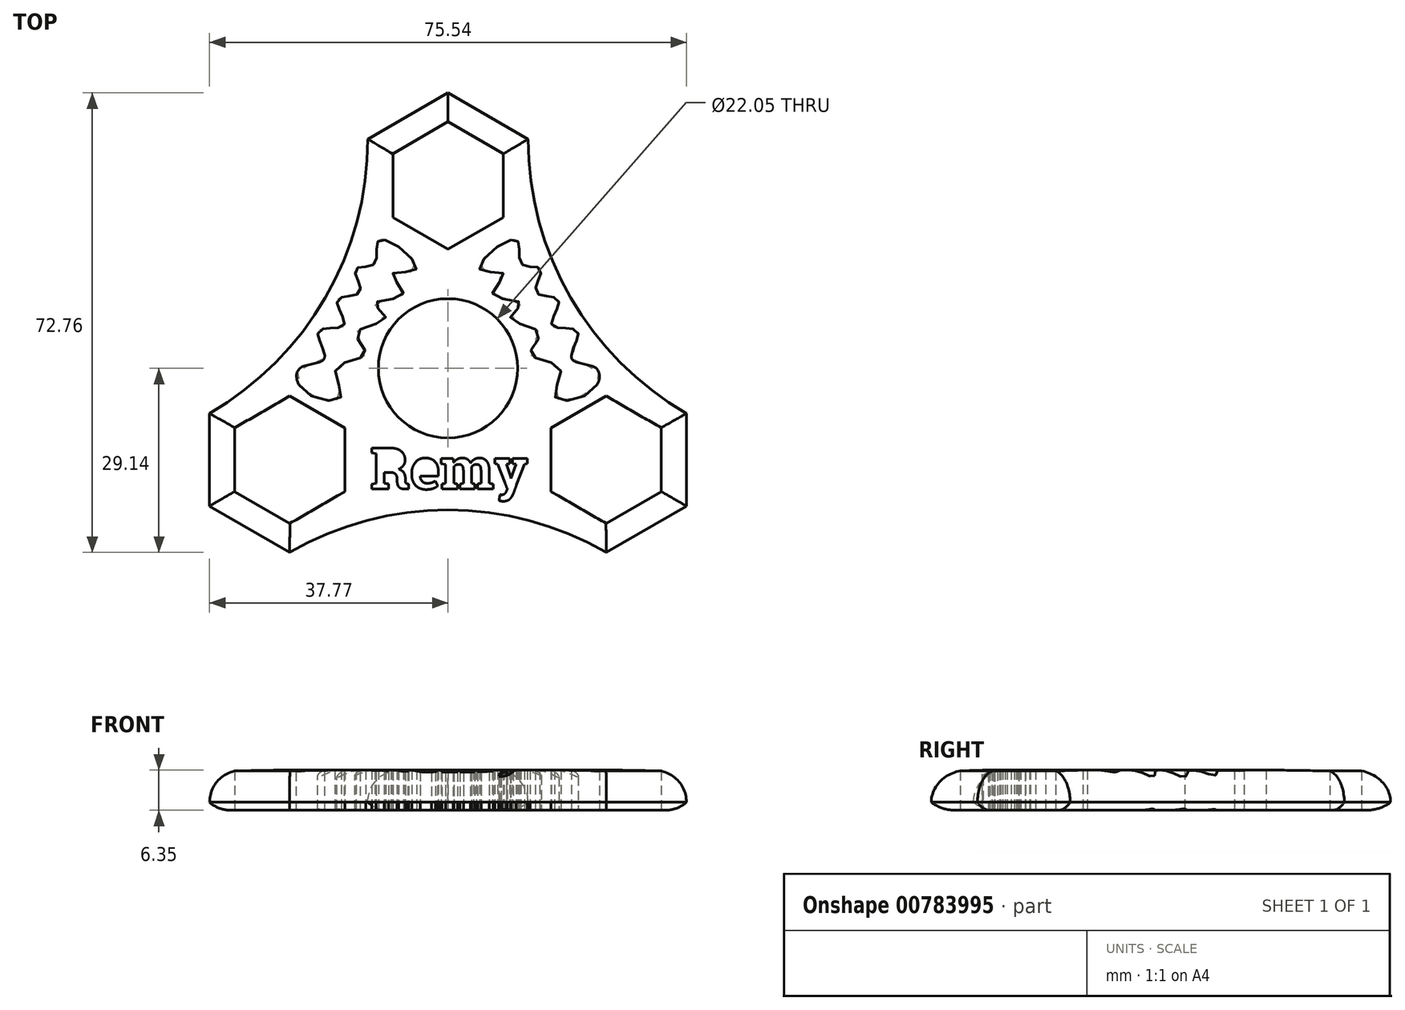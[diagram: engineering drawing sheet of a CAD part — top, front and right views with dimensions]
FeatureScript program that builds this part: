
annotation { "Feature Type Name" : "Feature", "Feature Type Description" : "" }
export const myFeature = defineFeature(function(context is Context, id is Id, definition is map)
    precondition{}
    {
        {
            var Q0;
            Q0=qCreatedBy(makeId("Top.planeOp"),FACE);
            var sketch = newSketch(context, id + "F0", { "sketchPlane" : qUnion([Q0])});
            skCircle(sketch, "E0", {"center": v(0, 0) * mm, "radius": 11.02 * mm});
            skCircle(sketch, "E1", {"center": v(0, 0) * mm, "radius": 14.29 * mm});
            skCircle(sketch, "E2.cCircle", {"center": v(0, 28.95) * mm, "radius": 8.73 * mm, "construction": true});
            skLineSegment(sketch, "E2.0", {"start": v(-8.73, 34) * mm, "end": v(0, 39.03) * mm});
            skLineSegment(sketch, "E2.1", {"start": v(0, 39.03) * mm, "end": v(8.73, 34) * mm});
            skLineSegment(sketch, "E2.2", {"start": v(8.73, 34) * mm, "end": v(8.73, 23.91) * mm});
            skLineSegment(sketch, "E2.3", {"start": v(8.73, 23.91) * mm, "end": v(0, 18.87) * mm});
            skLineSegment(sketch, "E2.4", {"start": v(0, 18.87) * mm, "end": v(-8.73, 23.91) * mm});
            skLineSegment(sketch, "E2.5", {"start": v(-8.73, 23.91) * mm, "end": v(-8.73, 34) * mm});
            skPoint(sketch, "E2.0.midPoint", {"position": v(-4.37, 36.51) * mm});
            skCircle(sketch, "E3.cCircle", {"center": v(0, 28.95) * mm, "radius": 12.7 * mm, "construction": true});
            skLineSegment(sketch, "E3.0", {"start": v(-12.7, 36.28) * mm, "end": v(0, 43.62) * mm});
            skLineSegment(sketch, "E3.1", {"start": v(0, 43.62) * mm, "end": v(12.7, 36.28) * mm});
            skLineSegment(sketch, "E3.2", {"start": v(12.7, 36.28) * mm, "end": v(12.7, 21.62) * mm});
            skLineSegment(sketch, "E3.3", {"start": v(12.7, 21.62) * mm, "end": v(0, 14.29) * mm});
            skLineSegment(sketch, "E3.4", {"start": v(0, 14.29) * mm, "end": v(-12.7, 21.62) * mm});
            skLineSegment(sketch, "E3.5", {"start": v(-12.7, 21.62) * mm, "end": v(-12.7, 36.28) * mm});
            skPoint(sketch, "E3.0.midPoint", {"position": v(-6.35, 39.95) * mm});
            skLineSegment(sketch, "E4.1.0", {"start": v(-37.77, -21.8) * mm, "end": v(-37.77, -7.14) * mm});
            skLineSegment(sketch, "E4.1.1", {"start": v(-25.07, 0.19) * mm, "end": v(-12.37, -7.14) * mm});
            skLineSegment(sketch, "E4.1.2", {"start": v(-16.34, -19.52) * mm, "end": v(-25.07, -24.56) * mm});
            skLineSegment(sketch, "E4.1.3", {"start": v(-12.37, -21.8) * mm, "end": v(-25.07, -29.14) * mm});
            skLineSegment(sketch, "E4.1.4", {"start": v(-37.77, -7.14) * mm, "end": v(-25.07, 0.19) * mm});
            skLineSegment(sketch, "E4.1.5", {"start": v(-33.8, -9.44) * mm, "end": v(-25.07, -4.4) * mm});
            skLineSegment(sketch, "E4.1.6", {"start": v(-33.8, -19.52) * mm, "end": v(-33.8, -9.44) * mm});
            skLineSegment(sketch, "E4.1.7", {"start": v(-25.07, -4.4) * mm, "end": v(-16.34, -9.44) * mm});
            skCircle(sketch, "E4.1.8", {"center": v(-25.07, -14.48) * mm, "radius": 12.7 * mm, "construction": true});
            skLineSegment(sketch, "E4.1.9", {"start": v(-25.07, -24.56) * mm, "end": v(-33.8, -19.52) * mm});
            skLineSegment(sketch, "E4.1.10", {"start": v(-16.34, -9.44) * mm, "end": v(-16.34, -19.52) * mm});
            skPoint(sketch, "E4.1.11", {"position": v(-31.42, -25.47) * mm});
            skCircle(sketch, "E4.1.12", {"center": v(-25.07, -14.48) * mm, "radius": 8.73 * mm, "construction": true});
            skLineSegment(sketch, "E4.1.13", {"start": v(-12.37, -7.14) * mm, "end": v(-12.37, -21.8) * mm});
            skPoint(sketch, "E4.1.14", {"position": v(-29.44, -22.04) * mm});
            skLineSegment(sketch, "E4.1.15", {"start": v(-25.07, -29.14) * mm, "end": v(-37.77, -21.8) * mm});
            skLineSegment(sketch, "E4.2.0", {"start": v(37.77, -21.8) * mm, "end": v(25.07, -29.14) * mm});
            skLineSegment(sketch, "E4.2.1", {"start": v(12.37, -21.8) * mm, "end": v(12.37, -7.14) * mm});
            skLineSegment(sketch, "E4.2.2", {"start": v(25.07, -4.4) * mm, "end": v(33.8, -9.44) * mm});
            skLineSegment(sketch, "E4.2.3", {"start": v(25.07, 0.19) * mm, "end": v(37.77, -7.14) * mm});
            skLineSegment(sketch, "E4.2.4", {"start": v(25.07, -29.14) * mm, "end": v(12.37, -21.8) * mm});
            skLineSegment(sketch, "E4.2.5", {"start": v(25.07, -24.56) * mm, "end": v(16.34, -19.52) * mm});
            skLineSegment(sketch, "E4.2.6", {"start": v(33.8, -19.52) * mm, "end": v(25.07, -24.56) * mm});
            skLineSegment(sketch, "E4.2.7", {"start": v(16.34, -19.52) * mm, "end": v(16.34, -9.44) * mm});
            skCircle(sketch, "E4.2.8", {"center": v(25.07, -14.48) * mm, "radius": 12.7 * mm, "construction": true});
            skLineSegment(sketch, "E4.2.9", {"start": v(33.8, -9.44) * mm, "end": v(33.8, -19.52) * mm});
            skLineSegment(sketch, "E4.2.10", {"start": v(16.34, -9.44) * mm, "end": v(25.07, -4.4) * mm});
            skPoint(sketch, "E4.2.11", {"position": v(37.77, -14.48) * mm});
            skCircle(sketch, "E4.2.12", {"center": v(25.07, -14.48) * mm, "radius": 8.73 * mm, "construction": true});
            skLineSegment(sketch, "E4.2.13", {"start": v(12.37, -7.14) * mm, "end": v(25.07, 0.19) * mm});
            skPoint(sketch, "E4.2.14", {"position": v(33.8, -14.48) * mm});
            skLineSegment(sketch, "E4.2.15", {"start": v(37.77, -7.14) * mm, "end": v(37.77, -21.8) * mm});
            skArc(sketch, "E5", {"start": v(-37.77, -7.14) * mm, "mid": v(-19.42, 11.21) * mm, "end": v(-12.7, 36.28) * mm});
            skArc(sketch, "E6", {"start": v(12.7, 36.28) * mm, "mid": v(19.42, 11.21) * mm, "end": v(37.77, -7.14) * mm});
            skArc(sketch, "E7", {"start": v(25.07, -29.14) * mm, "mid": v(0, -22.42) * mm, "end": v(-25.07, -29.14) * mm});
            skSolve(sketch);
        }
        {
            var Q0;
            Q0 = qSketchRegion(id + "F0", true);
            var Q1;
            Q1=makeQuery(id+"F0.imprint","IMPRINT",FACE,{"disambiguationData":[TD([[makeQuery(id+"F0.imprint","IMPRINT",EDGE,{"derivedFrom":sQuery(id+"F0.wireOp",EDGE,"E0")}),-1.0]])]});
            extrude(context, id + "F1", {"entities" : qUnion([Q0, Q1]), "depth" : 6.35 * mm, "offsetDistance" : 25.4 * mm});
        }
        {
            var Q0;
            Q0=qCreatedBy(makeId("Top.planeOp"),FACE);
            var sketch = newSketch(context, id + "F2", { "sketchPlane" : qUnion([Q0])});
            skText(sketch, "E8", { "text": "Remy", "fontName": "RobotoSlab-Bold.ttf"});
            const initialGuessF2  = {"E8": [-0.01232, -0.01911, 1, 0, 0.00657]};
            skSetInitialGuess(sketch, initialGuessF2);
            skSolve(sketch);
        }
        {
            var Q0;
            Q0 = qSketchRegion(id + "F2", true);
            extrude(context, id + "F3", {"entities" : qUnion([Q0]), "operationType" : NewBodyOperationType.REMOVE, "endBound" : BoundingType.THROUGH_ALL, "depth" : 25.4 * mm, "offsetDistance" : 25.4 * mm});
        }
        {
            var Q0;
            Q0=qCreatedBy(makeId("Top.planeOp"),FACE);
            var sketch = newSketch(context, id + "F4", { "sketchPlane" : qUnion([Q0])});
            skSolve(sketch);
        }
        {
            var Q0;
            Q0 = qSketchRegion(id + "F4", true);
            var Q1;
            Q1=makeQuery(id+"F3.boolean.opBoolean","SPLIT",FACE,{"disambiguationData":[TD([makeQuery(id+"F3.opExtrude","SWEPT_FACE",FACE,{"disambiguationData":[OSD([sQuery(id+"F2.wireOp",EDGE,"E8.sketch_text.stroke-29")])]})])],"derivedFrom":makeQuery(id+"F1.opExtrude","CAP_FACE",FACE,{"disambiguationData":[OSD([sQuery(id+"F0.wireOp",EDGE,"E0"),sQuery(id+"F0.wireOp",EDGE,"E2.0"),sQuery(id+"F0.wireOp",EDGE,"E2.1"),sQuery(id+"F0.wireOp",EDGE,"E2.2"),sQuery(id+"F0.wireOp",EDGE,"E2.3"),sQuery(id+"F0.wireOp",EDGE,"E2.4"),sQuery(id+"F0.wireOp",EDGE,"E2.5"),sQuery(id+"F0.wireOp",EDGE,"E3.0"),sQuery(id+"F0.wireOp",EDGE,"E3.1"),sQuery(id+"F0.wireOp",EDGE,"E4.1.0"),sQuery(id+"F0.wireOp",EDGE,"E4.1.2"),sQuery(id+"F0.wireOp",EDGE,"E4.1.5"),sQuery(id+"F0.wireOp",EDGE,"E4.1.6"),sQuery(id+"F0.wireOp",EDGE,"E4.1.7"),sQuery(id+"F0.wireOp",EDGE,"E4.1.9"),sQuery(id+"F0.wireOp",EDGE,"E4.1.10"),sQuery(id+"F0.wireOp",EDGE,"E4.1.15"),sQuery(id+"F0.wireOp",EDGE,"E4.2.0"),sQuery(id+"F0.wireOp",EDGE,"E4.2.2"),sQuery(id+"F0.wireOp",EDGE,"E4.2.5"),sQuery(id+"F0.wireOp",EDGE,"E4.2.6"),sQuery(id+"F0.wireOp",EDGE,"E4.2.7"),sQuery(id+"F0.wireOp",EDGE,"E4.2.9"),sQuery(id+"F0.wireOp",EDGE,"E4.2.10"),sQuery(id+"F0.wireOp",EDGE,"E4.2.15"),sQuery(id+"F0.wireOp",EDGE,"E5"),sQuery(id+"F0.wireOp",EDGE,"E6"),sQuery(id+"F0.wireOp",EDGE,"E7")])],"isStart":false})});
            extrude(context, id + "F5", {"entities" : qUnion([Q0, Q1]), "operationType" : NewBodyOperationType.REMOVE, "endBound" : BoundingType.THROUGH_ALL, "oppositeDirection" : true, "depth" : 25.4 * mm, "offsetDistance" : 25.4 * mm});
        }
        {
            var Q0;
            Q0=qCreatedBy(makeId("Top.planeOp"),FACE);
            var sketch = newSketch(context, id + "F6", { "sketchPlane" : qUnion([Q0])});
            skSolve(sketch);
        }
        {
            var Q0;
            Q0 = qSketchRegion(id + "F6", true);
            var Q1;
            Q1=makeQuery(id+"F3.boolean.opBoolean","SPLIT",FACE,{"disambiguationData":[TD([makeQuery(id+"F3.opExtrude","SWEPT_FACE",FACE,{"disambiguationData":[OSD([sQuery(id+"F2.wireOp",EDGE,"E8.sketch_text.stroke-53")])]})])],"derivedFrom":makeQuery(id+"F1.opExtrude","CAP_FACE",FACE,{"disambiguationData":[OSD([sQuery(id+"F0.wireOp",EDGE,"E0"),sQuery(id+"F0.wireOp",EDGE,"E2.0"),sQuery(id+"F0.wireOp",EDGE,"E2.1"),sQuery(id+"F0.wireOp",EDGE,"E2.2"),sQuery(id+"F0.wireOp",EDGE,"E2.3"),sQuery(id+"F0.wireOp",EDGE,"E2.4"),sQuery(id+"F0.wireOp",EDGE,"E2.5"),sQuery(id+"F0.wireOp",EDGE,"E3.0"),sQuery(id+"F0.wireOp",EDGE,"E3.1"),sQuery(id+"F0.wireOp",EDGE,"E4.1.0"),sQuery(id+"F0.wireOp",EDGE,"E4.1.2"),sQuery(id+"F0.wireOp",EDGE,"E4.1.5"),sQuery(id+"F0.wireOp",EDGE,"E4.1.6"),sQuery(id+"F0.wireOp",EDGE,"E4.1.7"),sQuery(id+"F0.wireOp",EDGE,"E4.1.9"),sQuery(id+"F0.wireOp",EDGE,"E4.1.10"),sQuery(id+"F0.wireOp",EDGE,"E4.1.15"),sQuery(id+"F0.wireOp",EDGE,"E4.2.0"),sQuery(id+"F0.wireOp",EDGE,"E4.2.2"),sQuery(id+"F0.wireOp",EDGE,"E4.2.5"),sQuery(id+"F0.wireOp",EDGE,"E4.2.6"),sQuery(id+"F0.wireOp",EDGE,"E4.2.7"),sQuery(id+"F0.wireOp",EDGE,"E4.2.9"),sQuery(id+"F0.wireOp",EDGE,"E4.2.10"),sQuery(id+"F0.wireOp",EDGE,"E4.2.15"),sQuery(id+"F0.wireOp",EDGE,"E5"),sQuery(id+"F0.wireOp",EDGE,"E6"),sQuery(id+"F0.wireOp",EDGE,"E7")])],"isStart":false})});
            extrude(context, id + "F7", {"entities" : qUnion([Q0, Q1]), "operationType" : NewBodyOperationType.REMOVE, "endBound" : BoundingType.THROUGH_ALL, "oppositeDirection" : true, "depth" : 25.4 * mm, "offsetDistance" : 25.4 * mm});
        }
        {
            var Q0;
            Q0=qCreatedBy(makeId("Top.planeOp"),FACE);
            var sketch = newSketch(context, id + "F8", { "sketchPlane" : qUnion([Q0])});
            skFitSpline(sketch, "E9", {"points": [v(-7.73, 19.18) * mm, v(-11.15, 20.05) * mm, v(-11.7, 16.48) * mm, v(-14.72, 15.68) * mm, v(-13.93, 12.03) * mm, v(-17.5, 10.84) * mm, v(-16.47, 6.79) * mm, v(-20.52, 5.91) * mm, v(-19.57, 1.62) * mm, v(-23.46, 0) * mm, v(-22.59, -3.78) * mm, v(-16.95, -4.5) * mm, v(-17.74, 0) * mm, v(-13.06, 2.26) * mm, v(-14.48, 5.6) * mm, v(-9.88, 7.98) * mm, v(-11.55, 10.28) * mm, v(-7.1, 11.71) * mm, v(-8.84, 14.89) * mm, v(-5.2, 15.52) * mm, v(-7.73, 19.18) * mm]});
            skFitSpline(sketch, "E10.MirrorC", {"points": [v(7.73, 19.18) * mm, v(11.15, 20.05) * mm, v(11.7, 16.48) * mm, v(14.72, 15.68) * mm, v(13.93, 12.03) * mm, v(17.5, 10.84) * mm, v(16.47, 6.79) * mm, v(20.52, 5.91) * mm, v(19.57, 1.62) * mm, v(23.46, 0) * mm, v(22.59, -3.78) * mm, v(16.95, -4.5) * mm, v(17.74, 0) * mm, v(13.06, 2.26) * mm, v(14.48, 5.6) * mm, v(9.88, 7.98) * mm, v(11.55, 10.28) * mm, v(7.1, 11.71) * mm, v(8.84, 14.89) * mm, v(5.2, 15.52) * mm, v(7.73, 19.18) * mm]});
            skSolve(sketch);
        }
        {
            var Q0;
            Q0 = qSketchRegion(id + "F8", true);
            extrude(context, id + "F9", {"entities" : qUnion([Q0]), "operationType" : NewBodyOperationType.REMOVE, "endBound" : BoundingType.THROUGH_ALL, "depth" : 25.4 * mm, "offsetDistance" : 25.4 * mm});
        }
        {
            var Q0;
            Q0=makeQuery(id+"F1.opExtrude","CAP_EDGE",EDGE,{"disambiguationData":[OSD([sQuery(id+"F0.wireOp",EDGE,"E5")])],"isStart":false});
            var Q1;
            Q1=makeQuery(id+"F1.opExtrude","CAP_EDGE",EDGE,{"disambiguationData":[OSD([sQuery(id+"F0.wireOp",EDGE,"E3.0")])],"isStart":false});
            var Q2;
            Q2=makeQuery(id+"F1.opExtrude","CAP_EDGE",EDGE,{"disambiguationData":[OSD([sQuery(id+"F0.wireOp",EDGE,"E3.1")])],"isStart":false});
            var Q3;
            Q3=makeQuery(id+"F1.opExtrude","CAP_EDGE",EDGE,{"disambiguationData":[OSD([sQuery(id+"F0.wireOp",EDGE,"E6")])],"isStart":false});
            var Q4;
            Q4=makeQuery(id+"F1.opExtrude","CAP_EDGE",EDGE,{"disambiguationData":[OSD([sQuery(id+"F0.wireOp",EDGE,"E4.2.15")])],"isStart":false});
            var Q5;
            Q5=makeQuery(id+"F1.opExtrude","CAP_EDGE",EDGE,{"disambiguationData":[OSD([sQuery(id+"F0.wireOp",EDGE,"E4.2.0")])],"isStart":false});
            var Q6;
            Q6=makeQuery(id+"F1.opExtrude","CAP_EDGE",EDGE,{"disambiguationData":[OSD([sQuery(id+"F0.wireOp",EDGE,"E7")])],"isStart":false});
            var Q7;
            Q7=makeQuery(id+"F1.opExtrude","CAP_EDGE",EDGE,{"disambiguationData":[OSD([sQuery(id+"F0.wireOp",EDGE,"E4.1.15")])],"isStart":false});
            var Q8;
            Q8=makeQuery(id+"F1.opExtrude","CAP_EDGE",EDGE,{"disambiguationData":[OSD([sQuery(id+"F0.wireOp",EDGE,"E4.1.0")])],"isStart":false});
            fillet(context, id + "F10", {"entities" : qUnion([Q0, Q1, Q2, Q3, Q4, Q5, Q6, Q7, Q8]), "radius" : 5.08 * mm, "tangentPropagation" : true, "allowEdgeOverflow" : false});
        }
        {
            var Q0;
            Q0=makeQuery(id+"F1.opExtrude","CAP_EDGE",EDGE,{"disambiguationData":[OSD([sQuery(id+"F0.wireOp",EDGE,"E6")])],"isStart":true});
            var Q1;
            Q1=makeQuery(id+"F1.opExtrude","CAP_EDGE",EDGE,{"disambiguationData":[OSD([sQuery(id+"F0.wireOp",EDGE,"E4.2.15")])],"isStart":true});
            var Q2;
            Q2=makeQuery(id+"F1.opExtrude","CAP_EDGE",EDGE,{"disambiguationData":[OSD([sQuery(id+"F0.wireOp",EDGE,"E4.2.0")])],"isStart":true});
            var Q3;
            Q3=makeQuery(id+"F1.opExtrude","CAP_EDGE",EDGE,{"disambiguationData":[OSD([sQuery(id+"F0.wireOp",EDGE,"E7")])],"isStart":true});
            var Q4;
            Q4=makeQuery(id+"F1.opExtrude","CAP_EDGE",EDGE,{"disambiguationData":[OSD([sQuery(id+"F0.wireOp",EDGE,"E4.1.15")])],"isStart":true});
            var Q5;
            Q5=makeQuery(id+"F1.opExtrude","CAP_EDGE",EDGE,{"disambiguationData":[OSD([sQuery(id+"F0.wireOp",EDGE,"E4.1.0")])],"isStart":true});
            var Q6;
            Q6=makeQuery(id+"F1.opExtrude","CAP_EDGE",EDGE,{"disambiguationData":[OSD([sQuery(id+"F0.wireOp",EDGE,"E5")])],"isStart":true});
            var Q7;
            Q7=makeQuery(id+"F1.opExtrude","CAP_EDGE",EDGE,{"disambiguationData":[OSD([sQuery(id+"F0.wireOp",EDGE,"E3.0")])],"isStart":true});
            var Q8;
            Q8=makeQuery(id+"F1.opExtrude","CAP_EDGE",EDGE,{"disambiguationData":[OSD([sQuery(id+"F0.wireOp",EDGE,"E3.1")])],"isStart":true});
            fillet(context, id + "F11", {"entities" : qUnion([Q0, Q1, Q2, Q3, Q4, Q5, Q6, Q7, Q8]), "radius" : 5.08 * mm, "tangentPropagation" : true, "allowEdgeOverflow" : false});
        }
    });
